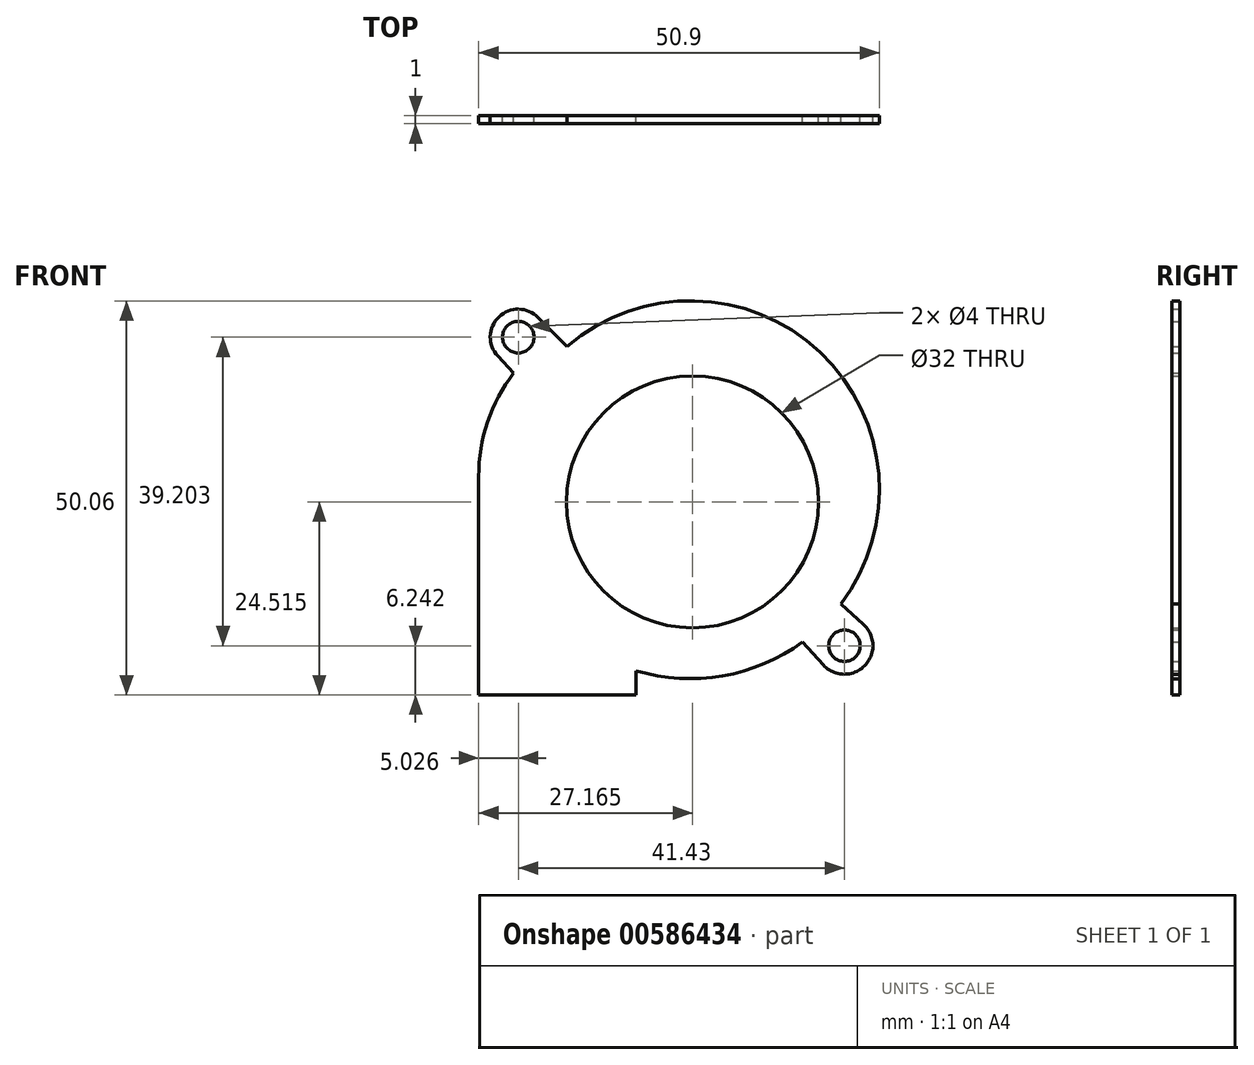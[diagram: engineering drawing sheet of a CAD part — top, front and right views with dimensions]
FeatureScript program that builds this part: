
annotation { "Feature Type Name" : "Feature", "Feature Type Description" : "" }
export const myFeature = defineFeature(function(context is Context, id is Id, definition is map)
    precondition{}
    {
        {
            var Q0;
            Q0=qCreatedBy(makeId("Front.planeOp"),FACE);
            var sketch = newSketch(context, id + "F0", { "sketchPlane" : qUnion([Q0])});
            skCircle(sketch, "E0", {"center": v(12.78, 22.35) * mm, "radius": 16 * mm, "construction": true});
            skPoint(sketch, "E0.first.point", {"position": v(12.7, 6.35) * mm});
            skPoint(sketch, "E0.second.point", {"position": v(-2.06, 28.32) * mm});
            skPoint(sketch, "E0.third.point", {"position": v(26, 31.38) * mm});
            skArc(sketch, "E1", {"start": v(4.2, 1.42) * mm, "mid": v(15.2, 0.76) * mm, "end": v(25.34, 5.08) * mm});
            skPoint(sketch, "E1.first.point", {"position": v(2, 46.61) * mm});
            skPoint(sketch, "E1.second.point", {"position": v(28.03, 41.43) * mm});
            skPoint(sketch, "E1.third.point", {"position": v(32.75, 14.02) * mm});
            skLineSegment(sketch, "E2", {"start": v(4.2, -2.65) * mm, "end": v(-15.8, -2.65) * mm, "construction": true});
            skLineSegment(sketch, "E3", {"start": v(-15.8, -2.65) * mm, "end": v(-15.8, 26.12) * mm});
            skLineSegment(sketch, "E4", {"start": v(4.2, -2.65) * mm, "end": v(4.2, 1.42) * mm});
            skCircle(sketch, "E5", {"center": v(-10.76, 43.8) * mm, "radius": 2 * mm});
            skCircle(sketch, "E6", {"center": v(30.67, 4.6) * mm, "radius": 2 * mm});
            skArc(sketch, "E7", {"start": v(-8.23, 46.29) * mm, "mid": v(-13.22, 46.36) * mm, "end": v(-13.36, 41.37) * mm});
            skArc(sketch, "E8", {"start": v(27.99, 2.16) * mm, "mid": v(33.23, 2.04) * mm, "end": v(33.09, 7.28) * mm});
            skLineSegment(sketch, "E9", {"start": v(33.09, 7.28) * mm, "end": v(30.21, 9.88) * mm});
            skLineSegment(sketch, "E10", {"start": v(27.99, 2.16) * mm, "end": v(25.34, 5.08) * mm});
            skArc(sketch, "E11.trimOffspring", {"start": v(-11.35, 39.2) * mm, "mid": v(-14.65, 33.03) * mm, "end": v(-15.8, 26.12) * mm});
            skArc(sketch, "E12.trimOffspring", {"start": v(30.21, 9.88) * mm, "mid": v(27.55, 41.9) * mm, "end": v(-4.57, 42.57) * mm});
            skLineSegment(sketch, "E13", {"start": v(-4.57, 42.57) * mm, "end": v(-8.23, 46.29) * mm});
            skLineSegment(sketch, "E14", {"start": v(-11.35, 39.2) * mm, "end": v(-13.36, 41.37) * mm});
            skLineSegment(sketch, "E15", {"start": v(-15.8, -1.65) * mm, "end": v(4.2, -1.65) * mm});
            skCircle(sketch, "E16", {"center": v(11.38, 22.87) * mm, "radius": 16 * mm});
            skLineSegment(sketch, "E17", {"start": v(12.78, 22.35) * mm, "end": v(21.8, 22.35) * mm, "construction": true});
            skLineSegment(sketch, "E18", {"start": v(12.78, 22.35) * mm, "end": v(11.38, 22.87) * mm, "construction": true});
            skSolve(sketch);
        }
        {
            var Q0;
            Q0=makeQuery(id+"F0.imprint","IMPRINT",FACE,{"disambiguationData":[TD([[makeQuery(id+"F0.imprint","IMPRINT",EDGE,{"derivedFrom":sQuery(id+"F0.wireOp",EDGE,"E0")}),-1.0]])]});
            var Q1;
            {var subQ1=sQuery(id+"F0.wireOp",EDGE,"E1");Q1=makeQuery(id+"F0.imprint","IMPRINT",FACE,{"disambiguationData":[TD([[makeQuery(id+"F0.imprint","IMPRINT",EDGE,{"derivedFrom":subQ1}),1.0]])]});}
            extrude(context, id + "F1", {"entities" : qUnion([Q0, Q1]), "depth" : 1 * mm, "offsetDistance" : 25.4 * mm});
        }
    });
